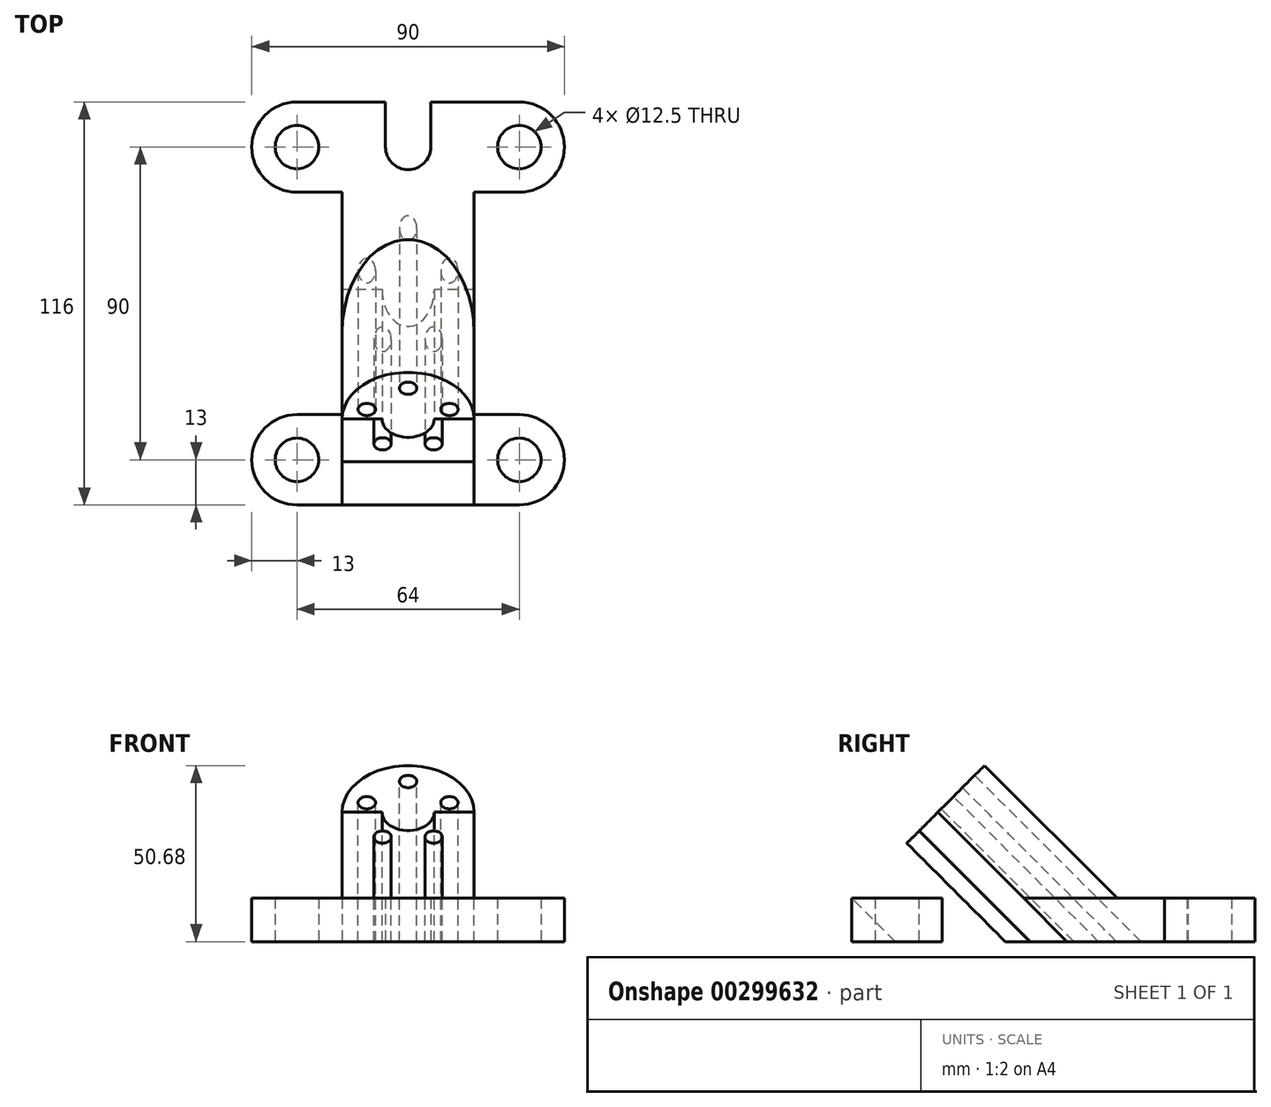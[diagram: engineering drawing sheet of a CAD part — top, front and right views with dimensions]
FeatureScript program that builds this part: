
annotation { "Feature Type Name" : "Feature", "Feature Type Description" : "" }
export const myFeature = defineFeature(function(context is Context, id is Id, definition is map)
    precondition{}
    {
        {
            var Q0;
            Q0=qCreatedBy(makeId("Top.planeOp"),FACE);
            var sketch = newSketch(context, id + "F0", { "sketchPlane" : qUnion([Q0])});
            skArc(sketch, "E0", {"start": v(-6.5, 0) * mm, "mid": v(0, -6.5) * mm, "end": v(6.5, 0) * mm});
            skLineSegment(sketch, "E1", {"start": v(6.5, 0) * mm, "end": v(6.5, 13) * mm});
            skLineSegment(sketch, "E2", {"start": v(-6.5, 0) * mm, "end": v(-6.5, 13) * mm});
            skLineSegment(sketch, "E3", {"start": v(43.77, 0) * mm, "end": v(-62.38, 0) * mm, "construction": true});
            skLineSegment(sketch, "E4", {"start": v(0, -7.06) * mm, "end": v(0, -160.36) * mm, "construction": true});
            skCircle(sketch, "E5", {"center": v(-32, 0) * mm, "radius": 6.25 * mm});
            skCircle(sketch, "E6", {"center": v(32, 0) * mm, "radius": 6.25 * mm});
            skArc(sketch, "E7", {"start": v(-32, 13) * mm, "mid": v(-45, 0) * mm, "end": v(-32, -13) * mm});
            skArc(sketch, "E8", {"start": v(32, -13) * mm, "mid": v(45, 0) * mm, "end": v(32, 13) * mm});
            skLineSegment(sketch, "E9", {"start": v(-32, 13) * mm, "end": v(-6.5, 13) * mm});
            skLineSegment(sketch, "E10", {"start": v(32, 13) * mm, "end": v(6.5, 13) * mm});
            skLineSegment(sketch, "E11", {"start": v(32, -13) * mm, "end": v(19, -13) * mm});
            skLineSegment(sketch, "E12", {"start": v(-32, -13) * mm, "end": v(-19, -13) * mm});
            skLineSegment(sketch, "E13", {"start": v(-19, -13) * mm, "end": v(-19, -77) * mm});
            skLineSegment(sketch, "E14", {"start": v(19, -13) * mm, "end": v(19, -77) * mm});
            skLineSegment(sketch, "E15", {"start": v(-19, -77) * mm, "end": v(-32, -77) * mm});
            skLineSegment(sketch, "E16", {"start": v(19, -77) * mm, "end": v(32, -77) * mm});
            skLineSegment(sketch, "E17", {"start": v(-32, 0) * mm, "end": v(-32, -142.73) * mm, "construction": true});
            skLineSegment(sketch, "E18", {"start": v(32, 0) * mm, "end": v(32, -155.44) * mm, "construction": true});
            skArc(sketch, "E19", {"start": v(32, -103) * mm, "mid": v(45, -90) * mm, "end": v(32, -77) * mm});
            skArc(sketch, "E20", {"start": v(-32, -77) * mm, "mid": v(-45, -90) * mm, "end": v(-32, -103) * mm});
            skCircle(sketch, "E21", {"center": v(-32, -90) * mm, "radius": 6.25 * mm});
            skCircle(sketch, "E22", {"center": v(32, -90) * mm, "radius": 6.25 * mm});
            skLineSegment(sketch, "E23", {"start": v(-32, -90) * mm, "end": v(44.47, -90) * mm, "construction": true});
            skLineSegment(sketch, "E24", {"start": v(-32, -103) * mm, "end": v(32, -103) * mm});
            skSolve(sketch);
        }
        {
            var Q0;
            Q0=makeQuery(id+"F0.imprint","IMPRINT",FACE,{"disambiguationData":[TD([[makeQuery(id+"F0.imprint","IMPRINT",EDGE,{"derivedFrom":sQuery(id+"F0.wireOp",EDGE,"E0")}),-1.0]])]});
            extrude(context, id + "F1", {"entities" : qUnion([Q0]), "depth" : 12.5 * mm});
        }
        {
            var Q0;
            Q0=qCreatedBy(makeId("Right.planeOp"),FACE);
            var sketch = newSketch(context, id + "F2", { "sketchPlane" : qUnion([Q0])});
            skLineSegment(sketch, "E25.0.0", {"start": v(-77, 0) * mm, "end": v(-13, 0) * mm});
            skLineSegment(sketch, "E25.0.1", {"start": v(-13, 0) * mm, "end": v(-13, 12.5) * mm});
            skLineSegment(sketch, "E25.0.2", {"start": v(-13, 12.5) * mm, "end": v(-77, 12.5) * mm});
            skLineSegment(sketch, "E25.0.3", {"start": v(-77, 12.5) * mm, "end": v(-77, 0) * mm});
            skLineSegment(sketch, "E26.0.0", {"start": v(-103, 0) * mm, "end": v(-77, 0) * mm});
            skLineSegment(sketch, "E26.0.1", {"start": v(-77, 0) * mm, "end": v(-77, 12.5) * mm});
            skLineSegment(sketch, "E26.0.2", {"start": v(-77, 12.5) * mm, "end": v(-103, 12.5) * mm});
            skLineSegment(sketch, "E26.0.3", {"start": v(-103, 12.5) * mm, "end": v(-103, 0) * mm});
            skLineSegment(sketch, "E27", {"start": v(-103, 12.5) * mm, "end": v(-53.5, 12.5) * mm});
            skLineSegment(sketch, "E28", {"start": v(-53.5, 12.5) * mm, "end": v(-78.25, 37.25) * mm});
            skLineSegment(sketch, "E29", {"start": v(-78.25, 37.25) * mm, "end": v(-103, 12.5) * mm});
            skSolve(sketch);
        }
        {
            var Q0;
            {var subQ3=sQuery(id+"F2.wireOp",EDGE,"E28");Q0=makeQuery(id+"F2.imprint","IMPRINT",FACE,{"disambiguationData":[TD([[makeQuery(id+"F2.imprint","IMPRINT",EDGE,{"derivedFrom":subQ3}),1.0]])]});}
            extrude(context, id + "F3", {"entities" : qUnion([Q0]), "operationType" : NewBodyOperationType.ADD, "depth" : 38 * mm, "symmetric" : true});
        }
        {
            var Q0;
            Q0=makeQuery(id+"F3.opExtrude","SWEPT_FACE",FACE,{"disambiguationData":[OSD([sQuery(id+"F2.wireOp",EDGE,"E29")])]});
            var sketch = newSketch(context, id + "F4", { "sketchPlane" : qUnion([Q0])});
            skLineSegment(sketch, "E30.0.0", {"start": v(-19, -29) * mm, "end": v(-19, -64) * mm});
            skLineSegment(sketch, "E30.0.1", {"start": v(-19, -64) * mm, "end": v(19, -64) * mm});
            skLineSegment(sketch, "E30.0.2", {"start": v(19, -64) * mm, "end": v(19, -29) * mm});
            skLineSegment(sketch, "E30.0.3", {"start": v(19, -29) * mm, "end": v(-19, -29) * mm});
            skArc(sketch, "E31", {"start": v(19, -29) * mm, "mid": v(0, -10) * mm, "end": v(-19, -29) * mm});
            skCircle(sketch, "E32", {"center": v(0, -29) * mm, "radius": 7.5 * mm});
            skCircle(sketch, "E33", {"center": v(0, -29) * mm, "radius": 12.5 * mm, "construction": true});
            skLineSegment(sketch, "E34", {"start": v(0, -29) * mm, "end": v(0, 2.45) * mm, "construction": true});
            skPoint(sketch, "E34.endSnap0", {"position": v(0, -10) * mm});
            skCircle(sketch, "E35", {"center": v(0, -16.5) * mm, "radius": 2.5 * mm});
            skLineSegment(sketch, "E36.0", {"start": v(-9.08, -16.5) * mm, "end": v(9.08, -16.5) * mm});
            skLineSegment(sketch, "E36.1", {"start": v(9.08, -16.5) * mm, "end": v(14.7, -33.77) * mm});
            skLineSegment(sketch, "E36.2", {"start": v(14.7, -33.77) * mm, "end": v(0, -44.44) * mm});
            skLineSegment(sketch, "E36.3", {"start": v(0, -44.44) * mm, "end": v(-14.7, -33.77) * mm});
            skLineSegment(sketch, "E36.4", {"start": v(-14.7, -33.77) * mm, "end": v(-9.08, -16.5) * mm});
            skCircle(sketch, "E37", {"center": v(11.89, -25.13) * mm, "radius": 2.5 * mm});
            skCircle(sketch, "E38", {"center": v(7.35, -39.1) * mm, "radius": 2.5 * mm});
            skCircle(sketch, "E39", {"center": v(-7.35, -39.1) * mm, "radius": 2.5 * mm});
            skCircle(sketch, "E40", {"center": v(-11.89, -25.13) * mm, "radius": 2.5 * mm});
            skSolve(sketch);
        }
        {
            var Q0;
            {var subQ4=sQuery(id+"F4.wireOp",EDGE,"E31");Q0=makeQuery(id+"F4.imprint","IMPRINT",FACE,{"disambiguationData":[TD([[makeQuery(id+"F4.imprint","IMPRINT",EDGE,{"derivedFrom":subQ4}),1.0]])]});}
            var Q1;
            Q1=makeQuery(id+"F4.imprint","IMPRINT",FACE,{"disambiguationData":[TD([[makeQuery(id+"F4.imprint","IMPRINT",EDGE,{"derivedFrom":sQuery(id+"F4.wireOp",EDGE,"E40")}),-1.0]])]});
            var Q2;
            {var subQ0=sQuery(id+"F4.wireOp",EDGE,"E32");var subQ1=sQuery(id+"F4.wireOp",EDGE,"E30.0.3");var subQ2=makeQuery(id+"F4.imprint","INTERSECT",VERTEX,{"disambiguationData":[OD(0.0)],"derivedFrom":[subQ1,subQ0]});Q2=makeQuery(id+"F4.imprint","IMPRINT",FACE,{"disambiguationData":[TD([[makeQuery(id+"F4.imprint","IMPRINT",EDGE,{"disambiguationData":[TD([[subQ2,-1.0]])],"derivedFrom":subQ1}),-1.0]])]});}
            var Q3;
            {var subQ0=sQuery(id+"F0.wireOp",EDGE,"E10");var subQ1=sQuery(id+"F0.wireOp",EDGE,"E9");var subQ2=sQuery(id+"F0.wireOp",EDGE,"E8");var subQ3=sQuery(id+"F0.wireOp",EDGE,"E7");var subQ5=sQuery(id+"F0.wireOp",EDGE,"E6");var subQ8=sQuery(id+"F0.wireOp",EDGE,"E11");var subQ9=sQuery(id+"F0.wireOp",EDGE,"E0");var subQ10=sQuery(id+"F0.wireOp",EDGE,"E5");var subQ11=sQuery(id+"F0.wireOp",EDGE,"E1");var subQ12=sQuery(id+"F0.wireOp",EDGE,"E2");var subQ13=sQuery(id+"F0.wireOp",EDGE,"E12");var subQ14=sQuery(id+"F0.wireOp",EDGE,"E13");var subQ15=sQuery(id+"F0.wireOp",EDGE,"E14");Q3=makeQuery(id+"F3.boolean.opBoolean","SPLIT",FACE,{"disambiguationData":[TD([makeQuery(id+"F1.opExtrude","SWEPT_FACE",FACE,{"disambiguationData":[OSD([subQ9])]})])],"derivedFrom":makeQuery(id+"F1.opExtrude","CAP_FACE",FACE,{"disambiguationData":[OSD([subQ9,subQ11,subQ12,subQ10,subQ5,subQ3,subQ2,subQ1,subQ0,subQ8,subQ13,subQ14,subQ15,sQuery(id+"F0.wireOp",EDGE,"E15"),sQuery(id+"F0.wireOp",EDGE,"E16"),sQuery(id+"F0.wireOp",EDGE,"E19"),sQuery(id+"F0.wireOp",EDGE,"E20"),sQuery(id+"F0.wireOp",EDGE,"E21"),sQuery(id+"F0.wireOp",EDGE,"E22"),sQuery(id+"F0.wireOp",EDGE,"E24")])],"isStart":false})});}
            extrude(context, id + "F5", {"entities" : qUnion([Q0, Q1, Q2]), "operationType" : NewBodyOperationType.ADD, "endBound" : BoundingType.UP_TO_SURFACE, "oppositeDirection" : true, "endBoundEntityFace" : qUnion([Q3]), "depth" : 25 * mm});
        }
        {
            var Q0;
            {var subQ0=sQuery(id+"F4.wireOp",EDGE,"E36.0");var subQ1=sQuery(id+"F4.wireOp",EDGE,"E35");var subQ2=makeQuery(id+"F4.imprint","INTERSECT",VERTEX,{"disambiguationData":[OD(0.0)],"derivedFrom":[subQ1,subQ0]});Q0=makeQuery(id+"F4.imprint","IMPRINT",FACE,{"disambiguationData":[TD([[makeQuery(id+"F4.imprint","IMPRINT",EDGE,{"disambiguationData":[TD([[subQ2,1.0]])],"derivedFrom":subQ1}),1.0]])]});}
            var Q1;
            {var subQ0=sQuery(id+"F4.wireOp",EDGE,"E36.0");var subQ1=sQuery(id+"F4.wireOp",EDGE,"E35");var subQ2=makeQuery(id+"F4.imprint","INTERSECT",VERTEX,{"disambiguationData":[OD(0.0)],"derivedFrom":[subQ1,subQ0]});Q1=makeQuery(id+"F4.imprint","IMPRINT",FACE,{"disambiguationData":[TD([[makeQuery(id+"F4.imprint","IMPRINT",EDGE,{"disambiguationData":[TD([[subQ2,-1.0]])],"derivedFrom":subQ1}),1.0]])]});}
            var Q2;
            {var subQ0=sQuery(id+"F4.wireOp",EDGE,"E37");var subQ1=sQuery(id+"F4.wireOp",EDGE,"E36.1");var subQ2=makeQuery(id+"F4.imprint","INTERSECT",VERTEX,{"disambiguationData":[OD(0.0)],"derivedFrom":[subQ1,subQ0]});Q2=makeQuery(id+"F4.imprint","IMPRINT",FACE,{"disambiguationData":[TD([[makeQuery(id+"F4.imprint","IMPRINT",EDGE,{"disambiguationData":[TD([[subQ2,-1.0]])],"derivedFrom":subQ1}),1.0]])]});}
            var Q3;
            {var subQ0=sQuery(id+"F4.wireOp",EDGE,"E37");var subQ1=sQuery(id+"F4.wireOp",EDGE,"E36.1");var subQ2=makeQuery(id+"F4.imprint","INTERSECT",VERTEX,{"disambiguationData":[OD(0.0)],"derivedFrom":[subQ1,subQ0]});Q3=makeQuery(id+"F4.imprint","IMPRINT",FACE,{"disambiguationData":[TD([[makeQuery(id+"F4.imprint","IMPRINT",EDGE,{"disambiguationData":[TD([[subQ2,-1.0]])],"derivedFrom":subQ1}),-1.0]])]});}
            var Q4;
            Q4=makeQuery(id+"F4.imprint","IMPRINT",FACE,{"disambiguationData":[TD([[makeQuery(id+"F4.imprint","IMPRINT",EDGE,{"derivedFrom":sQuery(id+"F4.wireOp",EDGE,"E40")}),1.0]])]});
            var Q5;
            {var subQ0=sQuery(id+"F4.wireOp",EDGE,"E39");var subQ1=sQuery(id+"F4.wireOp",EDGE,"E36.3");var subQ2=makeQuery(id+"F4.imprint","INTERSECT",VERTEX,{"disambiguationData":[OD(0.0)],"derivedFrom":[subQ1,subQ0]});Q5=makeQuery(id+"F4.imprint","IMPRINT",FACE,{"disambiguationData":[TD([[makeQuery(id+"F4.imprint","IMPRINT",EDGE,{"disambiguationData":[TD([[subQ2,-1.0]])],"derivedFrom":subQ1}),1.0]])]});}
            var Q6;
            {var subQ0=sQuery(id+"F4.wireOp",EDGE,"E39");var subQ1=sQuery(id+"F4.wireOp",EDGE,"E36.3");var subQ2=makeQuery(id+"F4.imprint","INTERSECT",VERTEX,{"disambiguationData":[OD(0.0)],"derivedFrom":[subQ1,subQ0]});Q6=makeQuery(id+"F4.imprint","IMPRINT",FACE,{"disambiguationData":[TD([[makeQuery(id+"F4.imprint","IMPRINT",EDGE,{"disambiguationData":[TD([[subQ2,-1.0]])],"derivedFrom":subQ1}),-1.0]])]});}
            var Q7;
            {var subQ0=sQuery(id+"F4.wireOp",EDGE,"E38");var subQ1=sQuery(id+"F4.wireOp",EDGE,"E36.2");var subQ2=makeQuery(id+"F4.imprint","INTERSECT",VERTEX,{"disambiguationData":[OD(0.0)],"derivedFrom":[subQ1,subQ0]});Q7=makeQuery(id+"F4.imprint","IMPRINT",FACE,{"disambiguationData":[TD([[makeQuery(id+"F4.imprint","IMPRINT",EDGE,{"disambiguationData":[TD([[subQ2,-1.0]])],"derivedFrom":subQ1}),1.0]])]});}
            var Q8;
            {var subQ0=sQuery(id+"F4.wireOp",EDGE,"E38");var subQ1=sQuery(id+"F4.wireOp",EDGE,"E36.2");var subQ2=makeQuery(id+"F4.imprint","INTERSECT",VERTEX,{"disambiguationData":[OD(0.0)],"derivedFrom":[subQ1,subQ0]});Q8=makeQuery(id+"F4.imprint","IMPRINT",FACE,{"disambiguationData":[TD([[makeQuery(id+"F4.imprint","IMPRINT",EDGE,{"disambiguationData":[TD([[subQ2,-1.0]])],"derivedFrom":subQ1}),-1.0]])]});}
            extrude(context, id + "F6", {"entities" : qUnion([Q0, Q1, Q2, Q3, Q4, Q5, Q6, Q7, Q8]), "operationType" : NewBodyOperationType.REMOVE, "endBound" : BoundingType.THROUGH_ALL, "oppositeDirection" : true, "depth" : 25 * mm});
        }
    });
